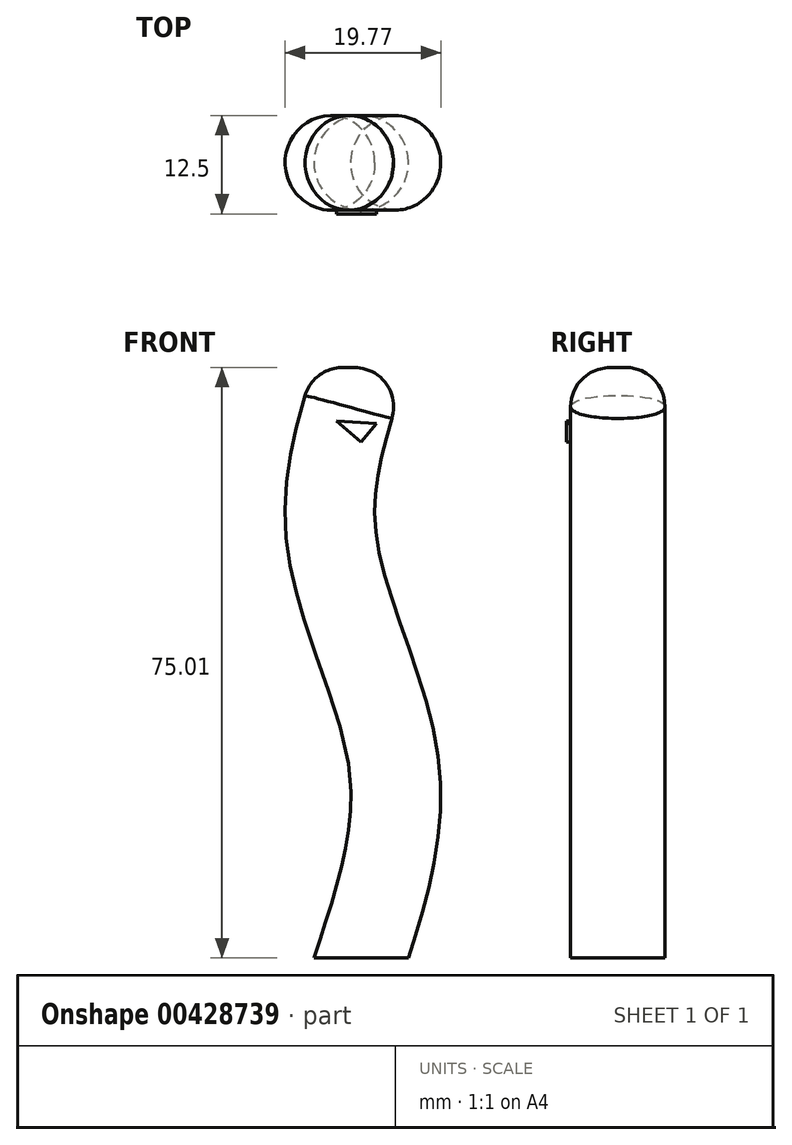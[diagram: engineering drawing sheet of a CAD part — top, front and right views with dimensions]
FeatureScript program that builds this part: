
annotation { "Feature Type Name" : "Feature", "Feature Type Description" : "" }
export const myFeature = defineFeature(function(context is Context, id is Id, definition is map)
    precondition{}
    {
        {
            var Q0;
            Q0=qCreatedBy(makeId("Top.planeOp"),FACE);
            var sketch = newSketch(context, id + "F0", { "sketchPlane" : qUnion([Q0])});
            skCircle(sketch, "E0", {"center": v(0, 0) * mm, "radius": 6 * mm});
            skSolve(sketch);
        }
        {
            var Q0;
            Q0=qCreatedBy(makeId("Front.planeOp"),FACE);
            var sketch = newSketch(context, id + "F1", { "sketchPlane" : qUnion([Q0])});
            skFitSpline(sketch, "E1", {"points": [v(0, 0) * mm, v(4.1, 24.59) * mm, v(-3.69, 52.87) * mm, v(0, 75) * mm], "startDerivative": vector(23.56, 72.86) * mm, "endDerivative": vector(22.44, 68.39) * mm});
            skSolve(sketch);
        }
        {
            var Q0;
            Q0=makeQuery(id+"F0.imprint","IMPRINT",FACE,{"disambiguationData":[TD([[makeQuery(id+"F0.imprint","IMPRINT",EDGE,{"derivedFrom":sQuery(id+"F0.wireOp",EDGE,"E0")}),1.0]])]});
            var Q1;
            Q1=sQuery(id+"F1.wireOp",EDGE,"E1");
            sweep(context, id + "F2", {"profiles" : qUnion([Q0]), "path" : qUnion([Q1])});
        }
        {
            var Q0;
            Q0=makeQuery(id+"F2.opSweep","CAP_FACE",FACE,{"disambiguationData":[OSD([sQuery(id+"F0.wireOp",EDGE,"E0"),sQuery(id+"F1.wireOp",VERTEX,"E1.end")])],"isStart":false});
            fillet(context, id + "F3", {"entities" : qUnion([Q0]), "radius" : 5 * mm, "tangentPropagation" : true, "allowEdgeOverflow" : false});
        }
        {
            var Q0;
            Q0=qCreatedBy(makeId("Front.planeOp"),FACE);
            cPlane(context, id + "F4", {"entities" : qUnion([Q0]), "cplaneType" : CPlaneType.OFFSET, "offset" : 6 * mm, "width" : 150 * mm, "height" : 150 * mm});
        }
        {
            var Q0;
            Q0=qCreatedBy(id+"F4.planeOp",FACE);
            var sketch = newSketch(context, id + "F5", { "sketchPlane" : qUnion([Q0])});
            skLineSegment(sketch, "E2", {"start": v(-3.13, 68.22) * mm, "end": v(0, 65.57) * mm});
            skLineSegment(sketch, "E3", {"start": v(0, 65.57) * mm, "end": v(1.96, 67.89) * mm});
            skLineSegment(sketch, "E4", {"start": v(1.96, 67.89) * mm, "end": v(-3.13, 68.22) * mm});
            skSolve(sketch);
        }
        {
            var Q0;
            Q0 = qSketchRegion(id + "F5", true);
            extrude(context, id + "F6", {"entities" : qUnion([Q0]), "operationType" : NewBodyOperationType.ADD, "depth" : 0.5 * mm});
        }
    });
